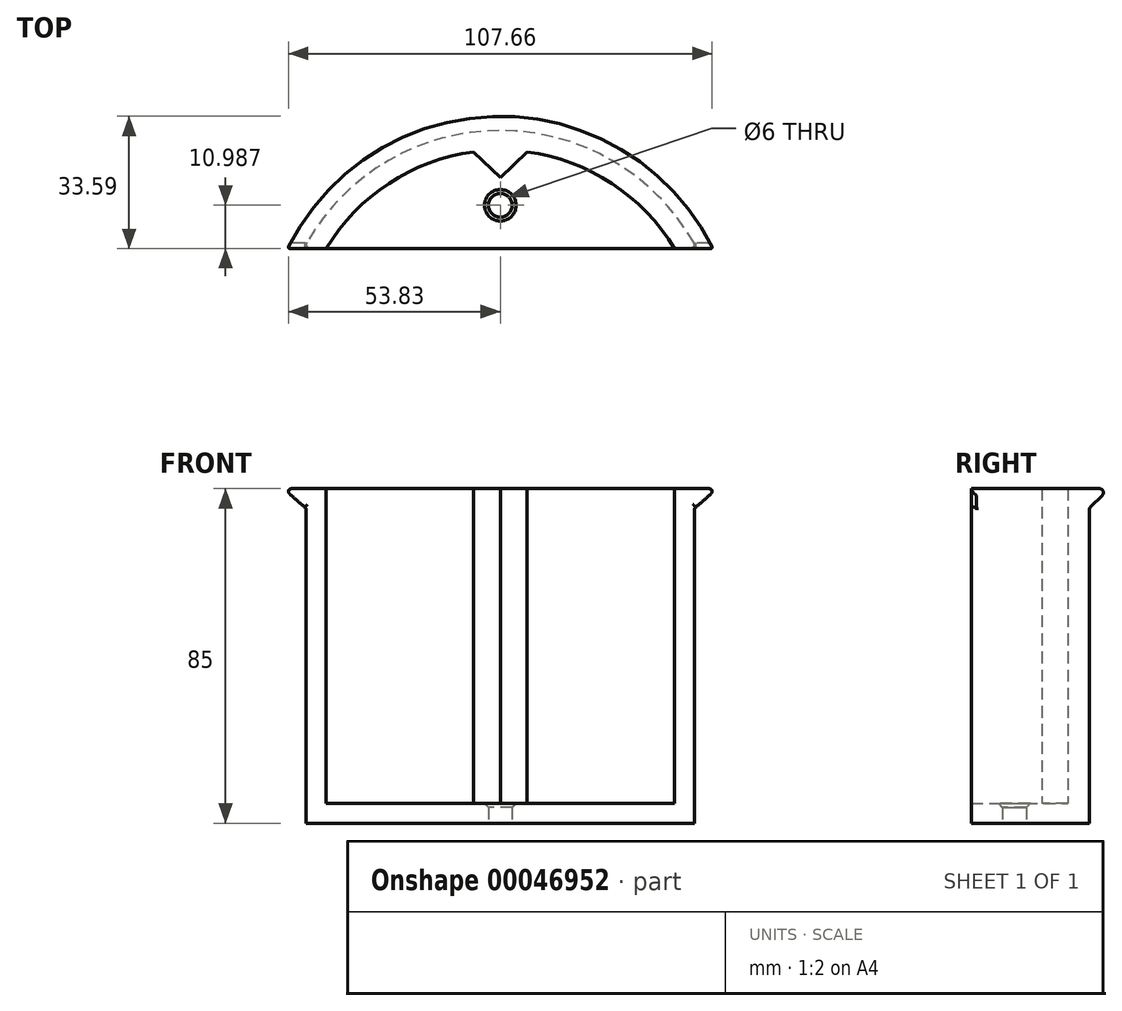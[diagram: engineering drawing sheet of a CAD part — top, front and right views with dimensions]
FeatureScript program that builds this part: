
annotation { "Feature Type Name" : "Feature", "Feature Type Description" : "" }
export const myFeature = defineFeature(function(context is Context, id is Id, definition is map)
    precondition{}
    {
        {
            var Q0;
            Q0=qCreatedBy(makeId("Top.planeOp"),FACE);
            var sketch = newSketch(context, id + "F0", { "sketchPlane" : qUnion([Q0])});
            skLineSegment(sketch, "E0.bottom", {"start": v(0, 0) * mm, "end": v(100, 0) * mm});
            skLineSegment(sketch, "E0.top", {"start": v(0, 30) * mm, "end": v(100, 30) * mm, "construction": true});
            skLineSegment(sketch, "E0.left", {"start": v(0, 0) * mm, "end": v(0, 30) * mm, "construction": true});
            skLineSegment(sketch, "E0.right", {"start": v(100, 0) * mm, "end": v(100, 30) * mm, "construction": true});
            skArc(sketch, "E1", {"start": v(50, 30) * mm, "mid": v(20.85, 21.92) * mm, "end": v(0, 0) * mm});
            skLineSegment(sketch, "E2", {"start": v(50, 30) * mm, "end": v(50, 0) * mm, "construction": true});
            skArc(sketch, "E3.MirrorCS", {"start": v(50, 30) * mm, "mid": v(79.15, 21.92) * mm, "end": v(100, 0) * mm});
            skArc(sketch, "E4.0", {"start": v(50, 25) * mm, "mid": v(24.59, 18.32) * mm, "end": v(5.75, 0) * mm});
            skArc(sketch, "E4.1", {"start": v(50, 25) * mm, "mid": v(75.41, 18.32) * mm, "end": v(94.25, 0) * mm});
            skCircle(sketch, "E5", {"center": v(50, 10.99) * mm, "radius": 3 * mm});
            skLineSegment(sketch, "E6", {"start": v(50, 18.02) * mm, "end": v(43.2, 24.55) * mm});
            skLineSegment(sketch, "E7.MirrorCS", {"start": v(50, 18.02) * mm, "end": v(56.8, 24.55) * mm});
            skSolve(sketch);
        }
        {
            var Q0;
            {var subQ1=sQuery(id+"F0.wireOp",EDGE,"E1");Q0=makeQuery(id+"F0.imprint","IMPRINT",FACE,{"disambiguationData":[TD([[makeQuery(id+"F0.imprint","IMPRINT",EDGE,{"derivedFrom":subQ1}),1.0]])]});}
            extrude(context, id + "F1", {"entities" : qUnion([Q0]), "depth" : 80 * mm});
        }
        {
            var Q0;
            {var subQ0=sQuery(id+"F0.wireOp",EDGE,"E4.0");Q0=makeQuery(id+"F0.imprint","IMPRINT",FACE,{"disambiguationData":[TD([[makeQuery(id+"F0.imprint","IMPRINT",EDGE,{"derivedFrom":subQ0}),1.0]])]});}
            var Q1;
            Q1=makeQuery(id+"F0.imprint","IMPRINT",FACE,{"disambiguationData":[TD([[makeQuery(id+"F0.imprint","IMPRINT",EDGE,{"derivedFrom":sQuery(id+"F0.wireOp",EDGE,"E5")}),-1.0]])]});
            extrude(context, id + "F2", {"entities" : qUnion([Q0, Q1]), "operationType" : NewBodyOperationType.ADD, "depth" : 5 * mm});
        }
        {
            var Q0;
            Q0=makeQuery(id+"F2.opExtrude","CAP_EDGE",EDGE,{"disambiguationData":[OSD([sQuery(id+"F0.wireOp",EDGE,"E5")])],"isStart":false});
            chamfer(context, id + "F3", {"entities" : qUnion([Q0]), "width" : 1 * mm, "tangentPropagation" : true});
        }
        {
            var Q0;
            {var subQ3=sQuery(id+"F0.wireOp",EDGE,"E6");Q0=makeQuery(id+"F0.imprint","IMPRINT",FACE,{"disambiguationData":[TD([[makeQuery(id+"F0.imprint","IMPRINT",EDGE,{"derivedFrom":subQ3}),-1.0]])]});}
            var Q1;
            Q1=makeQuery(id+"F1.opExtrude","CAP_FACE",FACE,{"disambiguationData":[OSD([sQuery(id+"F0.wireOp",EDGE,"E0.bottom"),sQuery(id+"F0.wireOp",EDGE,"E1"),sQuery(id+"F0.wireOp",EDGE,"E3.MirrorCS"),sQuery(id+"F0.wireOp",EDGE,"E4.0"),sQuery(id+"F0.wireOp",EDGE,"E4.1")])],"isStart":false});
            extrude(context, id + "F4", {"entities" : qUnion([Q0]), "operationType" : NewBodyOperationType.ADD, "endBound" : BoundingType.UP_TO_SURFACE, "endBoundEntityFace" : qUnion([Q1]), "depth" : 25 * mm});
        }
        {
            var Q0;
            {var subQ0=sQuery(id+"F0.wireOp",EDGE,"E4.1");var subQ1=sQuery(id+"F0.wireOp",EDGE,"E4.0");var subQ2=sQuery(id+"F0.wireOp",EDGE,"E3.MirrorCS");var subQ3=sQuery(id+"F0.wireOp",EDGE,"E1");var subQ4=sQuery(id+"F0.wireOp",EDGE,"E0.bottom");Q0=makeQuery(id+"F4.boolean.opBoolean","MERGE",FACE,{"derivedFrom":[makeQuery(id+"F1.opExtrude","CAP_FACE",FACE,{"disambiguationData":[OSD([subQ4,subQ3,subQ2,subQ1,subQ0])],"isStart":false}),makeQuery(id+"F4.opExtrude","CAP_FACE",FACE,{"disambiguationData":[OSD([subQ4,subQ3,subQ2,subQ1,subQ0])],"isStart":false})]});}
            var sketch = newSketch(context, id + "F5", { "sketchPlane" : qUnion([Q0])});
            skArc(sketch, "E8.0", {"start": v(105.6, 0) * mm, "mid": v(50, 35) * mm, "end": v(-5.6, 0) * mm});
            skLineSegment(sketch, "E9", {"start": v(0, 0) * mm, "end": v(-5.6, 0) * mm});
            skLineSegment(sketch, "E10", {"start": v(100, 0) * mm, "end": v(105.6, 0) * mm});
            skSolve(sketch);
        }
        {
            var Q0;
            Q0=makeQuery(id+"F5.imprint","IMPRINT",FACE,{"disambiguationData":[TD([[makeQuery(id+"F5.imprint","IMPRINT",EDGE,{"derivedFrom":sQuery(id+"F5.wireOp",EDGE,"E8.0")}),1.0]])]});
            var Q1;
            {var subQ2=sQuery(id+"F0.wireOp",EDGE,"E3.MirrorCS");var subQ3=sQuery(id+"F0.wireOp",EDGE,"E1");Q1=makeQuery(id+"F5.imprint","IMPRINT",FACE,{"disambiguationData":[TD([[makeQuery(id+"F5.imprint","IMPRINT",EDGE,{"derivedFrom":makeQuery(id+"F1.opExtrude","CAP_EDGE",EDGE,{"disambiguationData":[OSD([subQ3,subQ2])],"isStart":false})}),1.0]])]});}
            extrude(context, id + "F6", {"entities" : qUnion([Q0, Q1]), "operationType" : NewBodyOperationType.ADD, "depth" : 5 * mm});
        }
        {
            var Q0;
            Q0=makeQuery(id+"F6.opExtrude","CAP_EDGE",EDGE,{"disambiguationData":[OSD([sQuery(id+"F5.wireOp",EDGE,"E8.0")])],"isStart":true});
            chamfer(context, id + "F7", {"entities" : qUnion([Q0]), "width" : 5 * mm, "tangentPropagation" : true});
        }
        {
            var Q0;
            {var subQ0=sQuery(id+"F5.wireOp",EDGE,"E8.0");Q0=makeQuery(id+"F7.opChamfer","BLEND_EDGE",EDGE,{"blendedFrom":[makeQuery(id+"F6.opExtrude","CAP_EDGE",EDGE,{"disambiguationData":[OSD([subQ0])],"isStart":true}),makeQuery(id+"F6.opExtrude","CAP_FACE",FACE,{"disambiguationData":[OSD([sQuery(id+"F0.wireOp",EDGE,"E0.bottom"),sQuery(id+"F0.wireOp",EDGE,"E4.0"),sQuery(id+"F0.wireOp",EDGE,"E4.1"),sQuery(id+"F0.wireOp",EDGE,"E6"),sQuery(id+"F0.wireOp",EDGE,"E7.MirrorCS"),subQ0,sQuery(id+"F5.wireOp",EDGE,"E9"),sQuery(id+"F5.wireOp",EDGE,"E10")])],"isStart":false})],"blendedInto":[makeQuery(id+"F6.opExtrude","CAP_FACE",FACE,{"disambiguationData":[OSD([sQuery(id+"F0.wireOp",EDGE,"E0.bottom"),sQuery(id+"F0.wireOp",EDGE,"E4.0"),sQuery(id+"F0.wireOp",EDGE,"E4.1"),sQuery(id+"F0.wireOp",EDGE,"E6"),sQuery(id+"F0.wireOp",EDGE,"E7.MirrorCS"),subQ0,sQuery(id+"F5.wireOp",EDGE,"E9"),sQuery(id+"F5.wireOp",EDGE,"E10")])],"isStart":false})]});}
            var Q1;
            {var subQ0=sQuery(id+"F0.wireOp",EDGE,"E0.bottom");Q1=makeQuery(id+"F7.opChamfer","BLEND_EDGE",EDGE,{"disambiguationData":[OD(0.0)],"blendedFrom":[makeQuery(id+"F6.opExtrude","CAP_EDGE",EDGE,{"disambiguationData":[OSD([sQuery(id+"F5.wireOp",EDGE,"E8.0")])],"isStart":true}),makeQuery(id+"F6.boolean.opBoolean","MERGE",FACE,{"derivedFrom":[makeQuery(id+"F2.boolean.opBoolean","MERGE",FACE,{"derivedFrom":[makeQuery(id+"F1.opExtrude","SWEPT_FACE",FACE,{"disambiguationData":[OSD([subQ0]),TDD([makeQuery(id+"F0.imprint","IMPRINT",EDGE,{"disambiguationData":[TD([[makeQuery(id+"F0.imprint","INTERSECT",VERTEX,{"derivedFrom":[subQ0,sQuery(id+"F0.wireOp",EDGE,"E1")]}),-1.0]])],"derivedFrom":subQ0})])]}),makeQuery(id+"F1.opExtrude","SWEPT_FACE",FACE,{"disambiguationData":[OSD([subQ0]),TDD([makeQuery(id+"F0.imprint","IMPRINT",EDGE,{"disambiguationData":[TD([[makeQuery(id+"F0.imprint","INTERSECT",VERTEX,{"derivedFrom":[subQ0,sQuery(id+"F0.wireOp",EDGE,"E3.MirrorCS")]}),1.0]])],"derivedFrom":subQ0})])]}),makeQuery(id+"F2.opExtrude","SWEPT_FACE",FACE,{"disambiguationData":[OSD([subQ0])]})]}),makeQuery(id+"F6.opExtrude","SWEPT_FACE",FACE,{"disambiguationData":[OSD([subQ0,sQuery(id+"F5.wireOp",EDGE,"E9")])]}),makeQuery(id+"F6.opExtrude","SWEPT_FACE",FACE,{"disambiguationData":[OSD([subQ0,sQuery(id+"F5.wireOp",EDGE,"E10")])]})]})],"blendedInto":[makeQuery(id+"F6.boolean.opBoolean","MERGE",FACE,{"derivedFrom":[makeQuery(id+"F2.boolean.opBoolean","MERGE",FACE,{"derivedFrom":[makeQuery(id+"F1.opExtrude","SWEPT_FACE",FACE,{"disambiguationData":[OSD([subQ0]),TDD([makeQuery(id+"F0.imprint","IMPRINT",EDGE,{"disambiguationData":[TD([[makeQuery(id+"F0.imprint","INTERSECT",VERTEX,{"derivedFrom":[subQ0,sQuery(id+"F0.wireOp",EDGE,"E1")]}),-1.0]])],"derivedFrom":subQ0})])]}),makeQuery(id+"F1.opExtrude","SWEPT_FACE",FACE,{"disambiguationData":[OSD([subQ0]),TDD([makeQuery(id+"F0.imprint","IMPRINT",EDGE,{"disambiguationData":[TD([[makeQuery(id+"F0.imprint","INTERSECT",VERTEX,{"derivedFrom":[subQ0,sQuery(id+"F0.wireOp",EDGE,"E3.MirrorCS")]}),1.0]])],"derivedFrom":subQ0})])]}),makeQuery(id+"F2.opExtrude","SWEPT_FACE",FACE,{"disambiguationData":[OSD([subQ0])]})]}),makeQuery(id+"F6.opExtrude","SWEPT_FACE",FACE,{"disambiguationData":[OSD([subQ0,sQuery(id+"F5.wireOp",EDGE,"E9")])]}),makeQuery(id+"F6.opExtrude","SWEPT_FACE",FACE,{"disambiguationData":[OSD([subQ0,sQuery(id+"F5.wireOp",EDGE,"E10")])]})]})]});}
            var Q2;
            Q2=makeQuery(id+"F1.opExtrude","SWEPT_EDGE",EDGE,{"disambiguationData":[OSD([sQuery(id+"F0.wireOp",EDGE,"E0.bottom"),sQuery(id+"F0.wireOp",EDGE,"E1")])]});
            var Q3;
            {var subQ0=sQuery(id+"F0.wireOp",EDGE,"E0.bottom");Q3=makeQuery(id+"F7.opChamfer","BLEND_EDGE",EDGE,{"disambiguationData":[OD(1.0)],"blendedFrom":[makeQuery(id+"F6.opExtrude","CAP_EDGE",EDGE,{"disambiguationData":[OSD([sQuery(id+"F5.wireOp",EDGE,"E8.0")])],"isStart":true}),makeQuery(id+"F6.boolean.opBoolean","MERGE",FACE,{"derivedFrom":[makeQuery(id+"F2.boolean.opBoolean","MERGE",FACE,{"derivedFrom":[makeQuery(id+"F1.opExtrude","SWEPT_FACE",FACE,{"disambiguationData":[OSD([subQ0]),TDD([makeQuery(id+"F0.imprint","IMPRINT",EDGE,{"disambiguationData":[TD([[makeQuery(id+"F0.imprint","INTERSECT",VERTEX,{"derivedFrom":[subQ0,sQuery(id+"F0.wireOp",EDGE,"E1")]}),-1.0]])],"derivedFrom":subQ0})])]}),makeQuery(id+"F1.opExtrude","SWEPT_FACE",FACE,{"disambiguationData":[OSD([subQ0]),TDD([makeQuery(id+"F0.imprint","IMPRINT",EDGE,{"disambiguationData":[TD([[makeQuery(id+"F0.imprint","INTERSECT",VERTEX,{"derivedFrom":[subQ0,sQuery(id+"F0.wireOp",EDGE,"E3.MirrorCS")]}),1.0]])],"derivedFrom":subQ0})])]}),makeQuery(id+"F2.opExtrude","SWEPT_FACE",FACE,{"disambiguationData":[OSD([subQ0])]})]}),makeQuery(id+"F6.opExtrude","SWEPT_FACE",FACE,{"disambiguationData":[OSD([subQ0,sQuery(id+"F5.wireOp",EDGE,"E9")])]}),makeQuery(id+"F6.opExtrude","SWEPT_FACE",FACE,{"disambiguationData":[OSD([subQ0,sQuery(id+"F5.wireOp",EDGE,"E10")])]})]})],"blendedInto":[makeQuery(id+"F6.boolean.opBoolean","MERGE",FACE,{"derivedFrom":[makeQuery(id+"F2.boolean.opBoolean","MERGE",FACE,{"derivedFrom":[makeQuery(id+"F1.opExtrude","SWEPT_FACE",FACE,{"disambiguationData":[OSD([subQ0]),TDD([makeQuery(id+"F0.imprint","IMPRINT",EDGE,{"disambiguationData":[TD([[makeQuery(id+"F0.imprint","INTERSECT",VERTEX,{"derivedFrom":[subQ0,sQuery(id+"F0.wireOp",EDGE,"E1")]}),-1.0]])],"derivedFrom":subQ0})])]}),makeQuery(id+"F1.opExtrude","SWEPT_FACE",FACE,{"disambiguationData":[OSD([subQ0]),TDD([makeQuery(id+"F0.imprint","IMPRINT",EDGE,{"disambiguationData":[TD([[makeQuery(id+"F0.imprint","INTERSECT",VERTEX,{"derivedFrom":[subQ0,sQuery(id+"F0.wireOp",EDGE,"E3.MirrorCS")]}),1.0]])],"derivedFrom":subQ0})])]}),makeQuery(id+"F2.opExtrude","SWEPT_FACE",FACE,{"disambiguationData":[OSD([subQ0])]})]}),makeQuery(id+"F6.opExtrude","SWEPT_FACE",FACE,{"disambiguationData":[OSD([subQ0,sQuery(id+"F5.wireOp",EDGE,"E9")])]}),makeQuery(id+"F6.opExtrude","SWEPT_FACE",FACE,{"disambiguationData":[OSD([subQ0,sQuery(id+"F5.wireOp",EDGE,"E10")])]})]})]});}
            var Q4;
            Q4=makeQuery(id+"F1.opExtrude","SWEPT_EDGE",EDGE,{"disambiguationData":[OSD([sQuery(id+"F0.wireOp",EDGE,"E0.bottom"),sQuery(id+"F0.wireOp",EDGE,"E3.MirrorCS")])]});
            var Q5;
            Q5=makeQuery(id+"F7.opChamfer","BLEND_EDGE",EDGE,{"blendedFrom":[makeQuery(id+"F6.opExtrude","CAP_EDGE",EDGE,{"disambiguationData":[OSD([sQuery(id+"F5.wireOp",EDGE,"E8.0")])],"isStart":true}),makeQuery(id+"F1.opExtrude","SWEPT_FACE",FACE,{"disambiguationData":[OSD([sQuery(id+"F0.wireOp",EDGE,"E1"),sQuery(id+"F0.wireOp",EDGE,"E3.MirrorCS")])]})],"blendedInto":[makeQuery(id+"F1.opExtrude","SWEPT_FACE",FACE,{"disambiguationData":[OSD([sQuery(id+"F0.wireOp",EDGE,"E1"),sQuery(id+"F0.wireOp",EDGE,"E3.MirrorCS")])]})]});
            fillet(context, id + "F8", {"entities" : qUnion([Q0, Q1, Q2, Q3, Q4, Q5]), "radius" : 1 * mm, "tangentPropagation" : true, "allowEdgeOverflow" : false});
        }
    });
